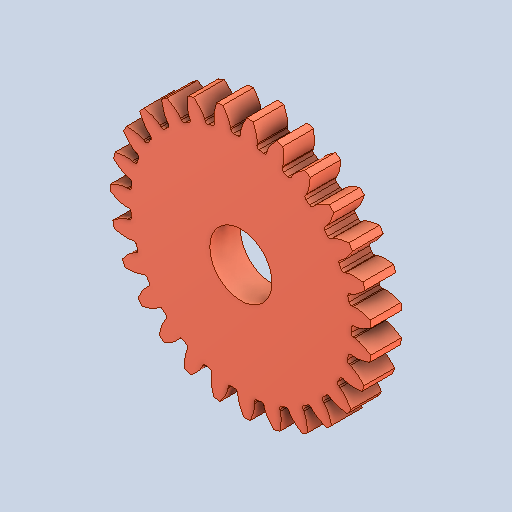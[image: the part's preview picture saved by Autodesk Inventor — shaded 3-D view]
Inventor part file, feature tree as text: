
AUTODESK INVENTOR PART (.ipt)
format: ipt  version: 2022 (Build 260153000, 153)  size: 462,848 bytes
history: imported  units: in
note: dims shown in document units (in); Inventor stores cm internally (conversion verified against a paired STEP export)
features: imported_body x1
ambient origin geometry x8: Origin, YZ Plane, XZ Plane, XY Plane, X Axis, Y Axis, Z Axis, Center Point
bodies: Solid1 (imported_parasolid), Body1 (imported_parasolid)
feature tree (1):
  imported_body  NMx_Import_Brep_tag  [imported B-rep: ~17 faces, bbox_mm=[8.277971, 8.292544, 3.1242]]
